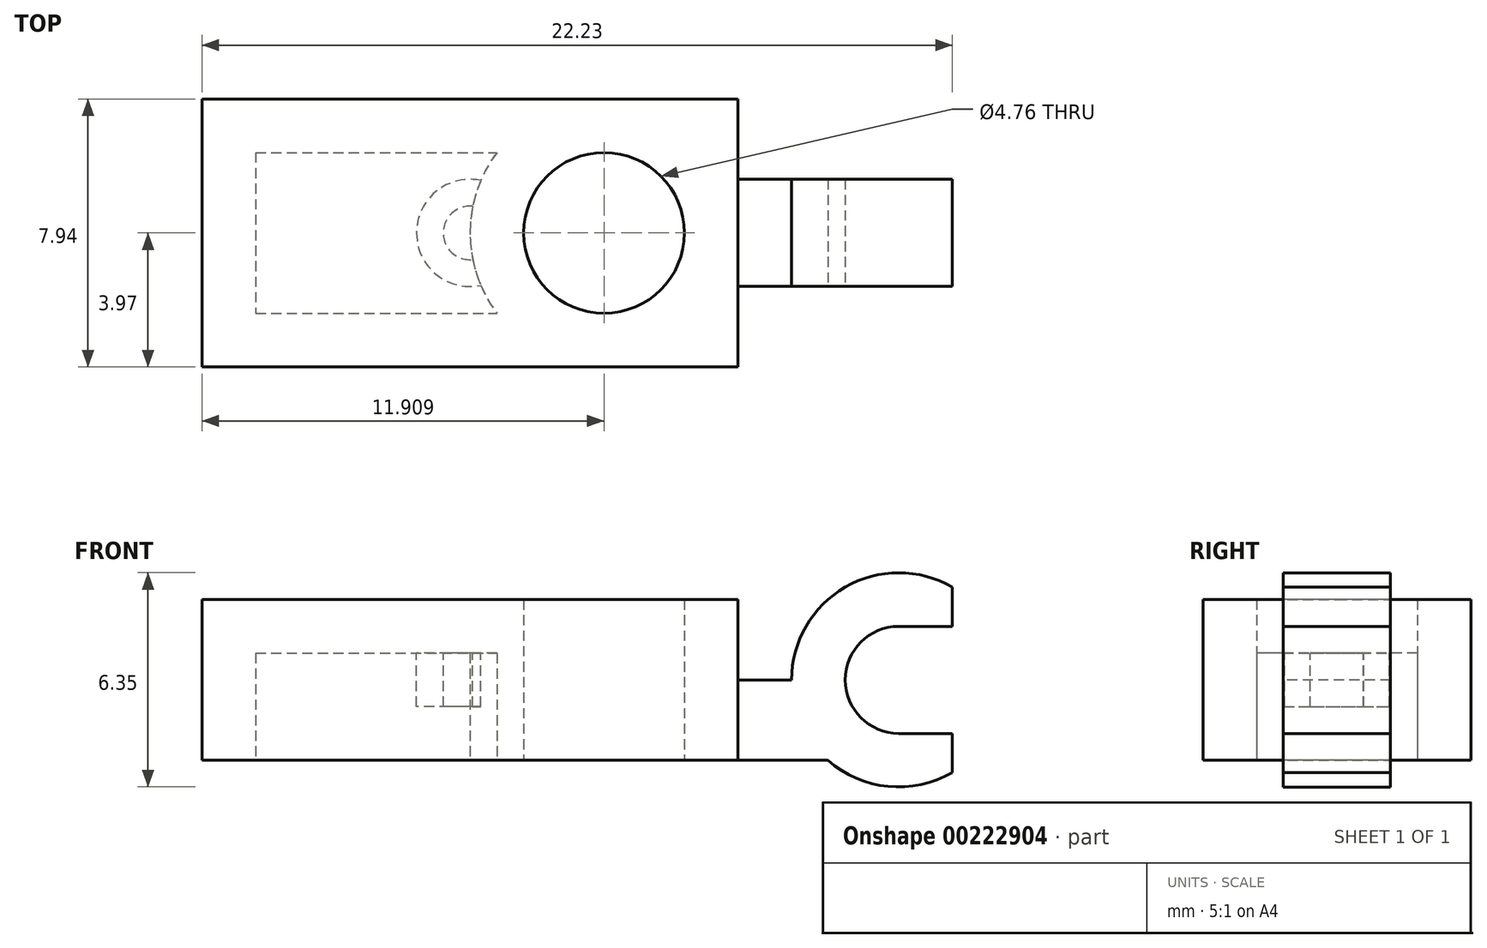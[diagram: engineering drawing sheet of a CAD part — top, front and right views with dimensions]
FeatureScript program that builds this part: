
annotation { "Feature Type Name" : "Feature", "Feature Type Description" : "" }
export const myFeature = defineFeature(function(context is Context, id is Id, definition is map)
    precondition{}
    {
        {
            var Q0;
            Q0=qCreatedBy(makeId("Top.planeOp"),FACE);
            var sketch = newSketch(context, id + "F0", { "sketchPlane" : qUnion([Q0])});
            skLineSegment(sketch, "E0.bottom", {"start": v(-7.94, 3.97) * mm, "end": v(7.94, 3.97) * mm});
            skLineSegment(sketch, "E0.top", {"start": v(-7.94, -3.97) * mm, "end": v(7.94, -3.97) * mm});
            skLineSegment(sketch, "E0.left", {"start": v(-7.94, 3.97) * mm, "end": v(-7.94, -3.97) * mm});
            skLineSegment(sketch, "E0.right", {"start": v(7.94, 3.97) * mm, "end": v(7.94, -3.97) * mm});
            skPoint(sketch, "E0.middle", {"position": v(0, 0) * mm});
            skCircle(sketch, "E1", {"center": v(-3.97, 0) * mm, "radius": 2.38 * mm});
            skCircle(sketch, "E2.MirrorC", {"center": v(3.97, 0) * mm, "radius": 2.38 * mm});
            skSolve(sketch);
        }
        {
            var Q0;
            Q0=makeQuery(id+"F0.imprint","IMPRINT",FACE,{"disambiguationData":[TD([[makeQuery(id+"F0.imprint","IMPRINT",EDGE,{"derivedFrom":sQuery(id+"F0.wireOp",EDGE,"E0.bottom")}),-1.0]])]});
            extrude(context, id + "F1", {"entities" : qUnion([Q0]), "depth" : 3.17 * mm});
        }
        {
            var Q0;
            Q0=makeQuery(id+"F0.imprint","IMPRINT",FACE,{"disambiguationData":[TD([[makeQuery(id+"F0.imprint","IMPRINT",EDGE,{"derivedFrom":sQuery(id+"F0.wireOp",EDGE,"E2.MirrorC")}),-1.0]])]});
            var Q1;
            Q1=makeQuery(id+"F0.imprint","IMPRINT",FACE,{"disambiguationData":[TD([[makeQuery(id+"F0.imprint","IMPRINT",EDGE,{"derivedFrom":sQuery(id+"F0.wireOp",EDGE,"E1")}),1.0]])]});
            extrude(context, id + "F2", {"entities" : qUnion([Q0, Q1]), "operationType" : NewBodyOperationType.ADD, "depth" : 4.76 * mm});
        }
        {
            var Q0;
            {var subQ0=sQuery(id+"F0.wireOp",EDGE,"E2.MirrorC");var subQ1=sQuery(id+"F0.wireOp",EDGE,"E1");Q0=makeQuery(id+"F2.boolean.opBoolean","MERGE",FACE,{"derivedFrom":[makeQuery(id+"F1.opExtrude","CAP_FACE",FACE,{"disambiguationData":[OSD([sQuery(id+"F0.wireOp",EDGE,"E0.bottom"),sQuery(id+"F0.wireOp",EDGE,"E0.top"),sQuery(id+"F0.wireOp",EDGE,"E0.left"),sQuery(id+"F0.wireOp",EDGE,"E0.right"),subQ1,subQ0])],"isStart":true}),makeQuery(id+"F2.opExtrude","CAP_FACE",FACE,{"disambiguationData":[OSD([subQ1])],"isStart":true}),makeQuery(id+"F2.opExtrude","CAP_FACE",FACE,{"disambiguationData":[OSD([subQ0])],"isStart":true})]});}
            shell(context, id + "F3", {"entities" : qUnion([Q0]), "thickness" : 1.59 * mm});
        }
        {
            var Q0;
            Q0=makeQuery(id+"F3.opShell","OFFSET_FACE",FACE,{"disambiguationData":[OSD([sQuery(id+"F0.wireOp",EDGE,"E0.bottom"),sQuery(id+"F0.wireOp",EDGE,"E0.top"),sQuery(id+"F0.wireOp",EDGE,"E0.left"),sQuery(id+"F0.wireOp",EDGE,"E0.right"),sQuery(id+"F0.wireOp",EDGE,"E1"),sQuery(id+"F0.wireOp",EDGE,"E2.MirrorC")])]});
            var sketch = newSketch(context, id + "F4", { "sketchPlane" : qUnion([Q0])});
            skCircle(sketch, "E3", {"center": v(0, 0) * mm, "radius": 1.59 * mm});
            skCircle(sketch, "E4", {"center": v(0, 0) * mm, "radius": 0.8 * mm});
            skSolve(sketch);
        }
        {
            var Q0;
            Q0=makeQuery(id+"F4.imprint","IMPRINT",FACE,{"disambiguationData":[TD([[makeQuery(id+"F4.imprint","IMPRINT",EDGE,{"derivedFrom":sQuery(id+"F4.wireOp",EDGE,"E3")}),1.0]])]});
            extrude(context, id + "F5", {"entities" : qUnion([Q0]), "operationType" : NewBodyOperationType.ADD, "depth" : 1.59 * mm});
        }
        {
            var Q0;
            Q0=makeQuery(id+"F1.opExtrude","SWEPT_FACE",FACE,{"disambiguationData":[OSD([sQuery(id+"F0.wireOp",EDGE,"E0.right")])]});
            var sketch = newSketch(context, id + "F6", { "sketchPlane" : qUnion([Q0])});
            skLineSegment(sketch, "E5", {"start": v(0, 0) * mm, "end": v(1.59, 0) * mm});
            skLineSegment(sketch, "E6", {"start": v(1.59, 0) * mm, "end": v(1.59, 6.35) * mm});
            skLineSegment(sketch, "E7", {"start": v(1.59, 6.35) * mm, "end": v(0, 6.35) * mm});
            skLineSegment(sketch, "E8", {"start": v(0, 6.35) * mm, "end": v(0, 0) * mm});
            skLineSegment(sketch, "E9.MirrorCS", {"start": v(-1.59, 6.35) * mm, "end": v(0, 6.35) * mm});
            skLineSegment(sketch, "E10.MirrorCS", {"start": v(-1.59, 0) * mm, "end": v(-1.59, 6.35) * mm});
            skLineSegment(sketch, "E11.MirrorCS", {"start": v(0, 0) * mm, "end": v(-1.59, 0) * mm});
            skSolve(sketch);
        }
        {
            var Q0;
            Q0 = qSketchRegion(id + "F6", true);
            extrude(context, id + "F7", {"entities" : qUnion([Q0]), "operationType" : NewBodyOperationType.ADD, "depth" : 4.76 * mm});
        }
        {
            var Q0;
            Q0=makeQuery(id+"F7.opExtrude","SWEPT_FACE",FACE,{"disambiguationData":[OSD([sQuery(id+"F6.wireOp",EDGE,"E10.MirrorCS")])]});
            var sketch = newSketch(context, id + "F8", { "sketchPlane" : qUnion([Q0])});
            skLineSegment(sketch, "E12", {"start": v(7.94, 3.17) * mm, "end": v(7.94, 2.38) * mm});
            skLineSegment(sketch, "E13", {"start": v(7.94, 2.38) * mm, "end": v(9.53, 2.38) * mm});
            skLineSegment(sketch, "E14", {"start": v(9.53, 2.38) * mm, "end": v(12.7, 2.38) * mm});
            skCircle(sketch, "E15", {"center": v(12.7, 2.38) * mm, "radius": 3.17 * mm});
            skCircle(sketch, "E16.0", {"center": v(12.7, 2.38) * mm, "radius": 1.59 * mm});
            skLineSegment(sketch, "E17", {"start": v(12.7, 0) * mm, "end": v(12.7, -0.8) * mm});
            skLineSegment(sketch, "E18", {"start": v(12.7, 0) * mm, "end": v(14.29, 0) * mm});
            skLineSegment(sketch, "E19", {"start": v(14.29, 0) * mm, "end": v(14.29, -0.37) * mm});
            skLineSegment(sketch, "E20", {"start": v(14.29, -0.37) * mm, "end": v(14.29, 5.13) * mm});
            skLineSegment(sketch, "E21", {"start": v(12.7, 0.8) * mm, "end": v(14.29, 0.8) * mm});
            skLineSegment(sketch, "E22", {"start": v(12.7, 3.97) * mm, "end": v(14.29, 3.97) * mm});
            skSolve(sketch);
        }
        {
            var Q0;
            {var subQ0=sQuery(id+"F8.wireOp",EDGE,"E17");Q0=makeQuery(id+"F8.imprint","IMPRINT",FACE,{"disambiguationData":[TD([[makeQuery(id+"F8.imprint","IMPRINT",EDGE,{"derivedFrom":subQ0}),-1.0]])]});}
            var Q1;
            {var subQ0=sQuery(id+"F8.wireOp",EDGE,"E17");Q1=makeQuery(id+"F8.imprint","IMPRINT",FACE,{"disambiguationData":[TD([[makeQuery(id+"F8.imprint","IMPRINT",EDGE,{"derivedFrom":subQ0}),1.0]])]});}
            var Q2;
            {var subQ5=sQuery(id+"F8.wireOp",EDGE,"E22");Q2=makeQuery(id+"F8.imprint","IMPRINT",FACE,{"disambiguationData":[TD([[makeQuery(id+"F8.imprint","IMPRINT",EDGE,{"derivedFrom":subQ5}),1.0]])]});}
            var Q3;
            {var subQ0=sQuery(id+"F8.wireOp",EDGE,"E18");Q3=makeQuery(id+"F8.imprint","IMPRINT",FACE,{"disambiguationData":[TD([[makeQuery(id+"F8.imprint","IMPRINT",EDGE,{"derivedFrom":subQ0}),1.0]])]});}
            extrude(context, id + "F9", {"entities" : qUnion([Q0, Q1, Q2, Q3]), "operationType" : NewBodyOperationType.ADD, "oppositeDirection" : true, "depth" : 3.17 * mm});
        }
        {
            var Q0;
            Q0=makeQuery(id+"F8.imprint","IMPRINT",FACE,{"disambiguationData":[TD([[makeQuery(id+"F8.imprint","IMPRINT",EDGE,{"derivedFrom":sQuery(id+"F8.wireOp",EDGE,"E12")}),-1.0]])]});
            var Q1;
            {var subQ0=sQuery(id+"F8.wireOp",EDGE,"E14");var subQ1=makeQuery(id+"F7.opExtrude","CAP_EDGE",EDGE,{"disambiguationData":[OSD([sQuery(id+"F6.wireOp",EDGE,"E10.MirrorCS")])],"isStart":false});var subQ2=makeQuery(id+"F8.imprint","INTERSECT",VERTEX,{"derivedFrom":[subQ1,subQ0]});Q1=makeQuery(id+"F8.imprint","IMPRINT",FACE,{"disambiguationData":[TD([[makeQuery(id+"F8.imprint","IMPRINT",EDGE,{"disambiguationData":[TD([[subQ2,1.0]])],"derivedFrom":subQ0}),-1.0]])]});}
            var Q2;
            {var subQ0=sQuery(id+"F8.wireOp",EDGE,"E14");var subQ1=makeQuery(id+"F7.opExtrude","CAP_EDGE",EDGE,{"disambiguationData":[OSD([sQuery(id+"F6.wireOp",EDGE,"E10.MirrorCS")])],"isStart":false});var subQ2=makeQuery(id+"F8.imprint","INTERSECT",VERTEX,{"derivedFrom":[subQ1,subQ0]});Q2=makeQuery(id+"F8.imprint","IMPRINT",FACE,{"disambiguationData":[TD([[makeQuery(id+"F8.imprint","IMPRINT",EDGE,{"disambiguationData":[TD([[subQ2,1.0]])],"derivedFrom":subQ0}),1.0]])]});}
            extrude(context, id + "F10", {"entities" : qUnion([Q0, Q1, Q2]), "operationType" : NewBodyOperationType.REMOVE, "oppositeDirection" : true, "depth" : 25.4 * mm});
        }
    });
